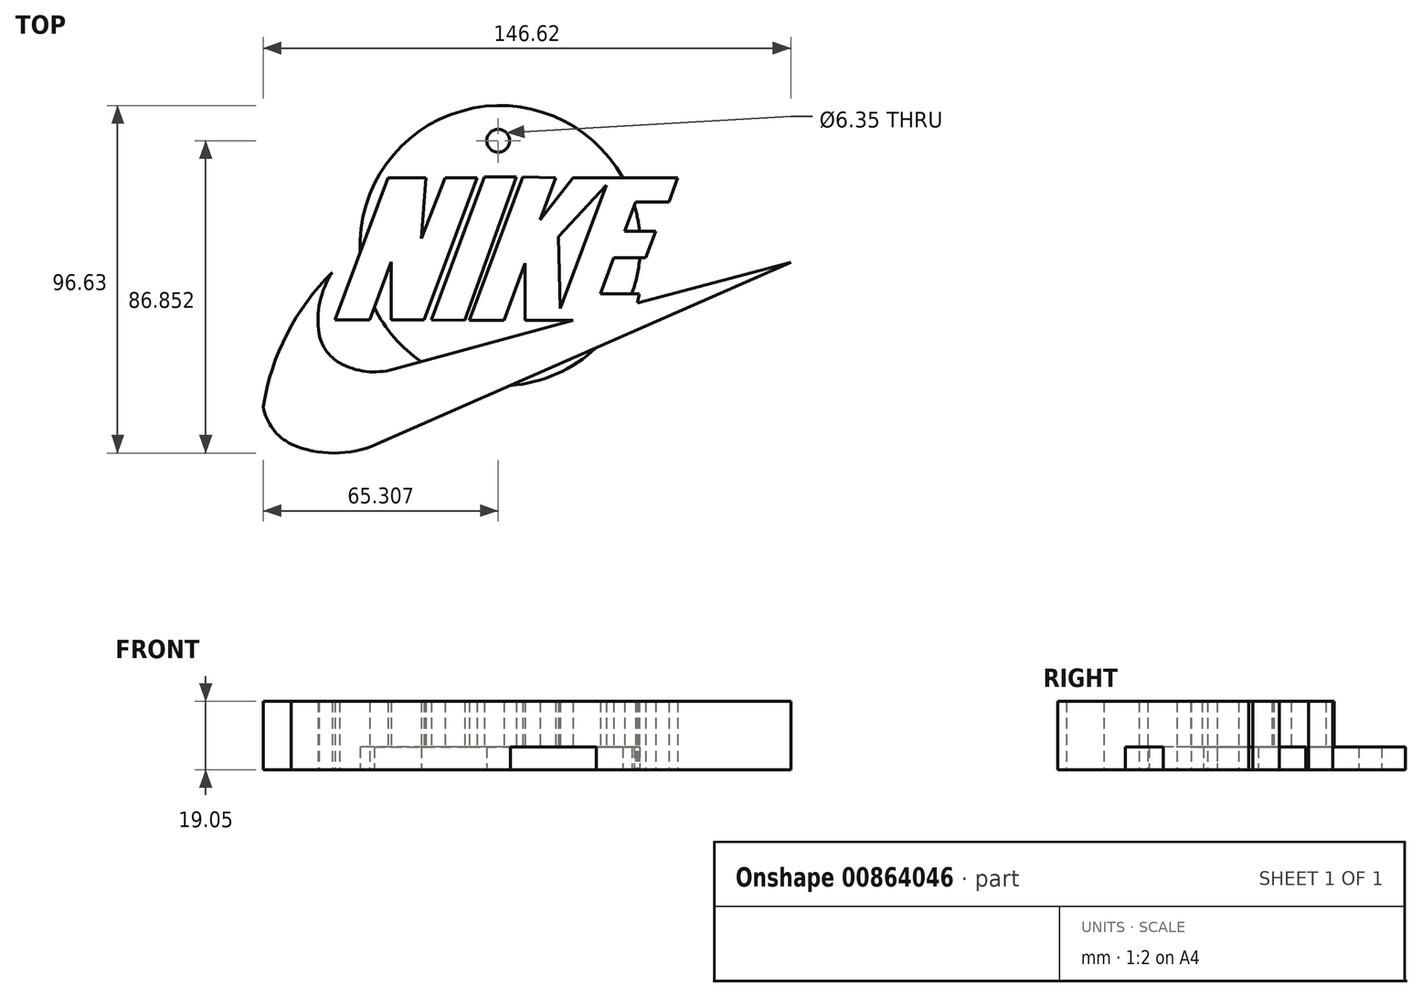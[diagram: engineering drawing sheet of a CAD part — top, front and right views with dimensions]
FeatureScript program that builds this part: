
annotation { "Feature Type Name" : "Feature", "Feature Type Description" : "" }
export const myFeature = defineFeature(function(context is Context, id is Id, definition is map)
    precondition{}
    {
        {
            var Q0;
            Q0=qCreatedBy(makeId("Top.planeOp"),FACE);
            var sketch = newSketch(context, id + "F0", { "sketchPlane" : qUnion([Q0])});
            skLineSegment(sketch, "E0", {"start": v(-57.25, 32.43) * mm, "end": v(-71.97, -7.06) * mm});
            skLineSegment(sketch, "E1", {"start": v(-71.97, -7.06) * mm, "end": v(-62.38, -7.06) * mm});
            skLineSegment(sketch, "E2", {"start": v(-62.38, -7.06) * mm, "end": v(-56.35, 9.12) * mm});
            skLineSegment(sketch, "E3", {"start": v(-56.35, 9.12) * mm, "end": v(-56.35, -7.06) * mm});
            skLineSegment(sketch, "E4", {"start": v(-56.35, -7.06) * mm, "end": v(-47.21, -7.06) * mm});
            skLineSegment(sketch, "E5", {"start": v(-47.21, -7.06) * mm, "end": v(-32.46, 32.5) * mm});
            skLineSegment(sketch, "E6", {"start": v(-32.04, 32.43) * mm, "end": v(-41.41, 32.43) * mm});
            skLineSegment(sketch, "E7", {"start": v(-41.41, 32.43) * mm, "end": v(-48.04, 15.53) * mm});
            skLineSegment(sketch, "E8", {"start": v(-48.04, 15.53) * mm, "end": v(-46.78, 32.43) * mm});
            skLineSegment(sketch, "E9", {"start": v(-46.78, 32.43) * mm, "end": v(-57.25, 32.43) * mm});
            skLineSegment(sketch, "E10", {"start": v(-21.51, 32.7) * mm, "end": v(-35.95, -7.18) * mm});
            skLineSegment(sketch, "E11", {"start": v(-35.95, -7.18) * mm, "end": v(-45.25, -7.06) * mm});
            skLineSegment(sketch, "E12", {"start": v(-21.51, 32.7) * mm, "end": v(-30.45, 32.7) * mm});
            skLineSegment(sketch, "E13", {"start": v(-30.45, 32.7) * mm, "end": v(-45.25, -7.06) * mm});
            skLineSegment(sketch, "E14", {"start": v(-10.66, 32.43) * mm, "end": v(-19.85, 32.7) * mm});
            skLineSegment(sketch, "E15", {"start": v(-19.85, 32.7) * mm, "end": v(-34.7, -7.18) * mm});
            skLineSegment(sketch, "E16", {"start": v(-34.7, -7.18) * mm, "end": v(-25.05, -7.18) * mm});
            skLineSegment(sketch, "E17", {"start": v(-25.05, -7.18) * mm, "end": v(-19.13, 8.73) * mm});
            skLineSegment(sketch, "E18", {"start": v(-19.13, 8.73) * mm, "end": v(-19.13, -7.18) * mm});
            skLineSegment(sketch, "E19", {"start": v(-19.13, -7.18) * mm, "end": v(-5.86, -7.18) * mm});
            skLineSegment(sketch, "E20", {"start": v(-10.66, 32.43) * mm, "end": v(-15, 20.77) * mm});
            skLineSegment(sketch, "E21", {"start": v(-15, 20.77) * mm, "end": v(-5.86, 32.43) * mm});
            skLineSegment(sketch, "E22", {"start": v(-5.86, 32.43) * mm, "end": v(23.32, 32.43) * mm});
            skLineSegment(sketch, "E23", {"start": v(23.32, 32.43) * mm, "end": v(20.81, 25.68) * mm});
            skLineSegment(sketch, "E24", {"start": v(20.81, 25.68) * mm, "end": v(11.53, 25.68) * mm});
            skLineSegment(sketch, "E25", {"start": v(11.53, 25.68) * mm, "end": v(8.5, 17.56) * mm});
            skLineSegment(sketch, "E26", {"start": v(8.5, 17.56) * mm, "end": v(17.13, 17.56) * mm});
            skLineSegment(sketch, "E27", {"start": v(17.13, 17.56) * mm, "end": v(14.37, 10.16) * mm});
            skLineSegment(sketch, "E28", {"start": v(14.37, 10.16) * mm, "end": v(5.53, 10.16) * mm});
            skLineSegment(sketch, "E29", {"start": v(5.53, 10.16) * mm, "end": v(1.84, 0.23) * mm});
            skLineSegment(sketch, "E30", {"start": v(1.84, 0.23) * mm, "end": v(12.58, 0.23) * mm});
            skLineSegment(sketch, "E31", {"start": v(12.58, 0.23) * mm, "end": v(12.04, -2.4) * mm});
            skLineSegment(sketch, "E32", {"start": v(12.04, -2.4) * mm, "end": v(54.7, 9) * mm});
            skLineSegment(sketch, "E33", {"start": v(54.7, 9) * mm, "end": v(-60.37, -41.61) * mm});
            skLineSegment(sketch, "E34", {"start": v(-9.36, -3.9) * mm, "end": v(3.4, 30.42) * mm});
            skLineSegment(sketch, "E35", {"start": v(3.4, 30.42) * mm, "end": v(-9.83, 16.02) * mm});
            skLineSegment(sketch, "E36", {"start": v(-9.83, 16.02) * mm, "end": v(-9.36, -3.9) * mm});
            skLineSegment(sketch, "E37", {"start": v(-5.86, -7.18) * mm, "end": v(-55.76, -20.83) * mm});
            skArc(sketch, "E38", {"start": v(-70.7, -19.06) * mm, "mid": v(-63.4, -21.4) * mm, "end": v(-55.76, -20.83) * mm});
            skArc(sketch, "E39", {"start": v(-76.47, -10.88) * mm, "mid": v(-74.47, -15.6) * mm, "end": v(-70.7, -19.06) * mm});
            skArc(sketch, "E40", {"start": v(-72.76, 6.15) * mm, "mid": v(-76.16, -2.03) * mm, "end": v(-76.47, -10.88) * mm});
            skArc(sketch, "E41", {"start": v(-84.13, -41.61) * mm, "mid": v(-72.25, -44.1) * mm, "end": v(-60.37, -41.61) * mm});
            skArc(sketch, "E42", {"start": v(-91.92, -31.23) * mm, "mid": v(-89.27, -37.35) * mm, "end": v(-84.13, -41.61) * mm});
            skArc(sketch, "E43", {"start": v(-72.76, 6.15) * mm, "mid": v(-85.36, -11) * mm, "end": v(-91.92, -31.23) * mm});
            skSolve(sketch);
        }
        {
            var Q0;
            Q0=qCreatedBy(makeId("Top.planeOp"),FACE);
            var sketch = newSketch(context, id + "F1", { "sketchPlane" : qUnion([Q0])});
            skCircle(sketch, "E44", {"center": v(-26.08, 13.56) * mm, "radius": 38.96 * mm});
            skPoint(sketch, "E45", {"position": v(-26.61, 42.74) * mm});
            skSolve(sketch);
        }
        {
            var Q0;
            Q0=makeQuery(id+"F0.imprint","IMPRINT",FACE,{"disambiguationData":[TD([[makeQuery(id+"F0.imprint","IMPRINT",EDGE,{"derivedFrom":sQuery(id+"F0.wireOp",EDGE,"E0")}),1.0]])]});
            var Q1;
            Q1=makeQuery(id+"F0.imprint","IMPRINT",FACE,{"disambiguationData":[TD([[makeQuery(id+"F0.imprint","IMPRINT",EDGE,{"derivedFrom":sQuery(id+"F0.wireOp",EDGE,"E10")}),-1.0]])]});
            var Q2;
            Q2=makeQuery(id+"F0.imprint","IMPRINT",FACE,{"disambiguationData":[TD([[makeQuery(id+"F0.imprint","IMPRINT",EDGE,{"derivedFrom":sQuery(id+"F0.wireOp",EDGE,"E14")}),1.0]])]});
            extrude(context, id + "F2", {"entities" : qUnion([Q0, Q1, Q2]), "depth" : 19.05 * mm, "offsetDistance" : 25.4 * mm});
        }
        {
            var Q0;
            Q0 = qSketchRegion(id + "F1", true);
            extrude(context, id + "F3", {"entities" : qUnion([Q0]), "operationType" : NewBodyOperationType.ADD, "depth" : 6.35 * mm, "offsetDistance" : 25.4 * mm});
        }
        {
            var Q0;
            Q0=sQuery(id+"F1.wireOp",VERTEX,"E45");
            var Q1;
            Q1=makeQuery(id+"F3.opExtrude","SWEPT_BODY",BODY,{"disambiguationData":[OSD([sQuery(id+"F1.wireOp",EDGE,"E44")])]});
            var Q2;
            Q2=makeQuery(id+"F2.opExtrude","SWEPT_BODY",BODY,{"disambiguationData":[OSD([sQuery(id+"F0.wireOp",EDGE,"E10"),sQuery(id+"F0.wireOp",EDGE,"E11"),sQuery(id+"F0.wireOp",EDGE,"E12"),sQuery(id+"F0.wireOp",EDGE,"E13")])]});
            var Q3;
            Q3=makeQuery(id+"F2.opExtrude","SWEPT_BODY",BODY,{"disambiguationData":[OSD([sQuery(id+"F0.wireOp",EDGE,"E0"),sQuery(id+"F0.wireOp",EDGE,"E1"),sQuery(id+"F0.wireOp",EDGE,"E2"),sQuery(id+"F0.wireOp",EDGE,"E3"),sQuery(id+"F0.wireOp",EDGE,"E4"),sQuery(id+"F0.wireOp",EDGE,"E5"),sQuery(id+"F0.wireOp",EDGE,"E6"),sQuery(id+"F0.wireOp",EDGE,"E7"),sQuery(id+"F0.wireOp",EDGE,"E8"),sQuery(id+"F0.wireOp",EDGE,"E9")])]});
            hole(context, id + "F4", {"style" : HoleStyle.SIMPLE, "endStyle" : HoleEndStyle.THROUGH, "oppositeDirection" : true, "holeDiameter" : 6.35 * mm, "majorDiameter" : 6.35 * mm, "isTappedThrough" : true, "tappedDepth" : 12.7 * mm, "tapClearance" : 3, "locations" : qUnion([Q0]), "scope" : qUnion([Q1, Q2, Q3])});
        }
    });
